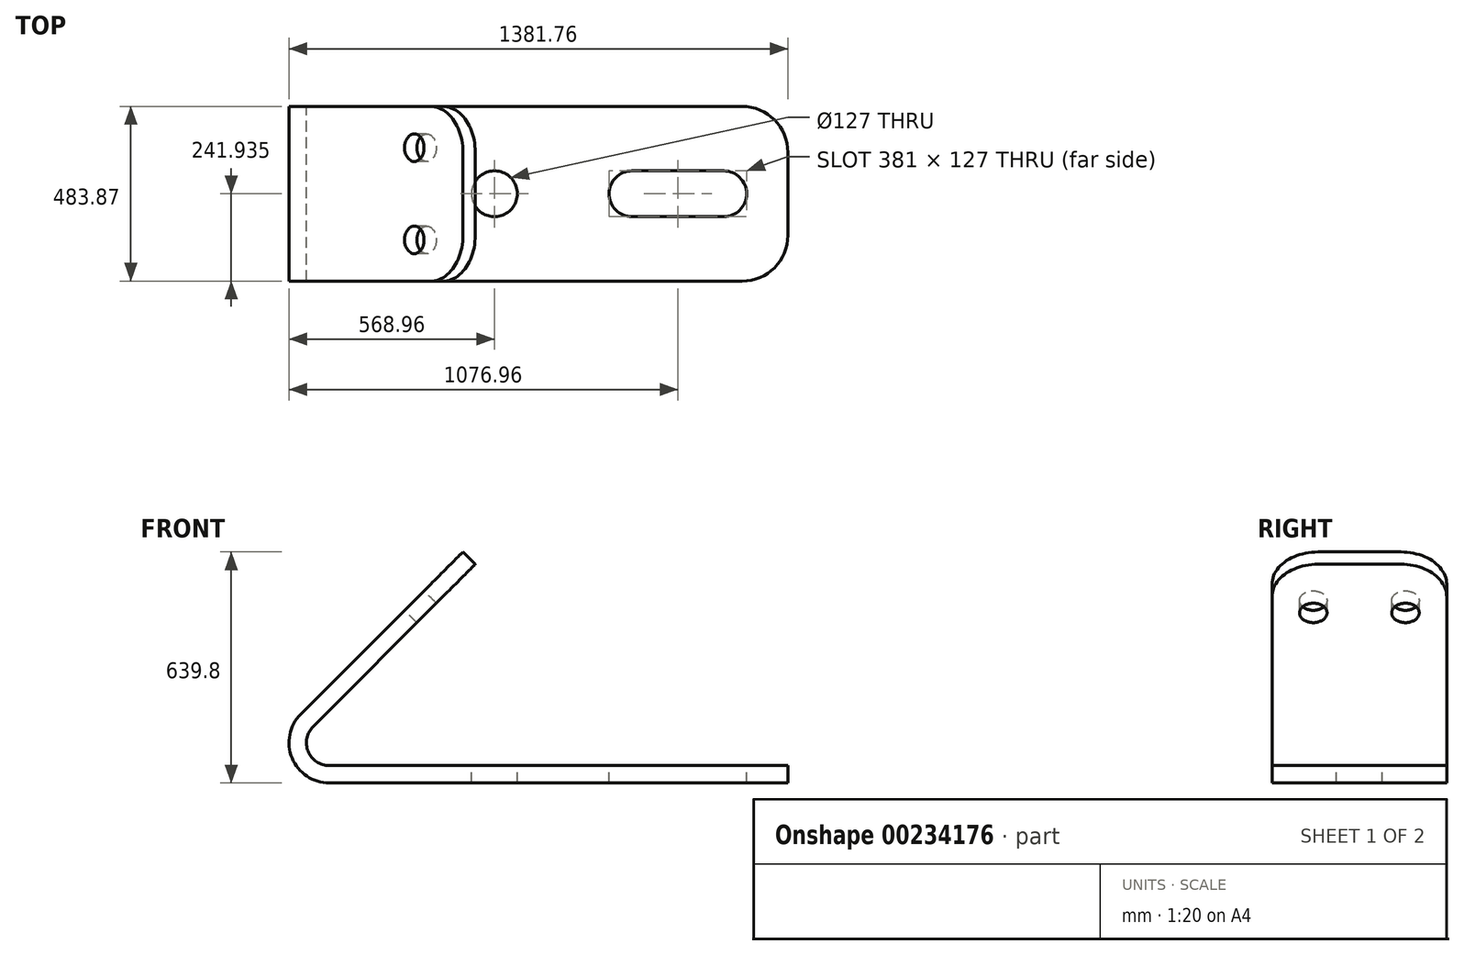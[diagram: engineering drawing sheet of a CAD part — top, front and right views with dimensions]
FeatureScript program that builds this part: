
annotation { "Feature Type Name" : "Feature", "Feature Type Description" : "" }
export const myFeature = defineFeature(function(context is Context, id is Id, definition is map)
    precondition{}
    {
        {
            var Q0;
            Q0=qCreatedBy(makeId("Front.planeOp"),FACE);
            var sketch = newSketch(context, id + "F0", { "sketchPlane" : qUnion([Q0])});
            skLineSegment(sketch, "E0", {"start": v(0, 0) * mm, "end": v(1270, 0) * mm});
            skLineSegment(sketch, "E1", {"start": v(1270, 0) * mm, "end": v(1270, 48.26) * mm});
            skLineSegment(sketch, "E2", {"start": v(1270, 48.26) * mm, "end": v(0, 48.26) * mm});
            skLineSegment(sketch, "E3", {"start": v(0, 0) * mm, "end": v(0, 111.76) * mm, "construction": true});
            skArc(sketch, "E4", {"start": v(-79.03, 190.79) * mm, "mid": v(-103.25, 69) * mm, "end": v(0, 0) * mm});
            skLineSegment(sketch, "E5", {"start": v(-79.03, 190.79) * mm, "end": v(369.99, 639.8) * mm});
            skLineSegment(sketch, "E6", {"start": v(369.99, 639.8) * mm, "end": v(404.11, 605.67) * mm});
            skArc(sketch, "E7", {"start": v(-44.9, 156.66) * mm, "mid": v(-58.67, 87.46) * mm, "end": v(0, 48.26) * mm});
            skLineSegment(sketch, "E8", {"start": v(404.11, 605.67) * mm, "end": v(-44.9, 156.66) * mm});
            skSolve(sketch);
        }
        {
            var Q0;
            Q0=qSketchRegion(id+"F0",true);
            extrude(context, id + "F1", {"entities" : qUnion([Q0]), "depth" : 483.87 * mm});
        }
        {
            var Q0;
            Q0=makeQuery(id+"F1.opExtrude","SWEPT_FACE",FACE,{"disambiguationData":[OSD([sQuery(id+"F0.wireOp",EDGE,"E5")])]});
            var sketch = newSketch(context, id + "F2", { "sketchPlane" : qUnion([Q0])});
            skCircle(sketch, "E9", {"center": v(114.3, 523.53) * mm, "radius": 38.1 * mm});
            skCircle(sketch, "E10", {"center": v(369.57, 523.53) * mm, "radius": 38.1 * mm});
            skSolve(sketch);
        }
        {
            var Q0;
            Q0=qSketchRegion(id+"F2",true);
            var Q1;
            Q1=makeQuery(id+"F1.opExtrude","SWEPT_FACE",FACE,{"disambiguationData":[OSD([sQuery(id+"F0.wireOp",EDGE,"E8")])]});
            extrude(context, id + "F3", {"entities" : qUnion([Q0]), "operationType" : NewBodyOperationType.REMOVE, "endBound" : BoundingType.UP_TO_SURFACE, "oppositeDirection" : true, "endBoundEntityFace" : qUnion([Q1]), "depth" : 25.4 * mm});
        }
        {
            var Q0;
            Q0=makeQuery(id+"F1.opExtrude","CAP_EDGE",EDGE,{"disambiguationData":[OSD([sQuery(id+"F0.wireOp",EDGE,"E6")])],"isStart":true});
            var Q1;
            Q1=makeQuery(id+"F1.opExtrude","CAP_EDGE",EDGE,{"disambiguationData":[OSD([sQuery(id+"F0.wireOp",EDGE,"E6")])],"isStart":false});
            fillet(context, id + "F4", {"entities" : qUnion([Q0, Q1]), "radius" : 127 * mm, "tangentPropagation" : true, "allowEdgeOverflow" : false});
        }
        {
            var Q0;
            Q0=makeQuery(id+"F1.opExtrude","SWEPT_FACE",FACE,{"disambiguationData":[OSD([sQuery(id+"F0.wireOp",EDGE,"E2")])]});
            var sketch = newSketch(context, id + "F5", { "sketchPlane" : qUnion([Q0])});
            skLineSegment(sketch, "E11", {"start": v(457.2, -241.94) * mm, "end": v(1270, -241.94) * mm, "construction": true});
            skCircle(sketch, "E12", {"center": v(457.2, -241.94) * mm, "radius": 63.5 * mm});
            skArc(sketch, "E13", {"start": v(1092.2, -305.44) * mm, "mid": v(1155.7, -241.94) * mm, "end": v(1092.2, -178.44) * mm});
            skLineSegment(sketch, "E14", {"start": v(1092.2, -178.44) * mm, "end": v(965.2, -178.44) * mm});
            skLineSegment(sketch, "E15", {"start": v(1092.2, -305.44) * mm, "end": v(965.2, -305.44) * mm});
            skLineSegment(sketch, "E16", {"start": v(965.2, -305.44) * mm, "end": v(965.2, -77.54) * mm, "construction": true});
            skLineSegment(sketch, "E17.MirrorCS", {"start": v(838.2, -178.44) * mm, "end": v(965.2, -178.44) * mm});
            skArc(sketch, "E18.MirrorCS", {"start": v(838.2, -305.44) * mm, "mid": v(774.7, -241.94) * mm, "end": v(838.2, -178.44) * mm});
            skLineSegment(sketch, "E19.MirrorCS", {"start": v(838.2, -305.44) * mm, "end": v(965.2, -305.44) * mm});
            skSolve(sketch);
        }
        {
            var Q0;
            Q0=qSketchRegion(id+"F5",true);
            extrude(context, id + "F6", {"entities" : qUnion([Q0]), "operationType" : NewBodyOperationType.REMOVE, "endBound" : BoundingType.THROUGH_ALL, "oppositeDirection" : true, "depth" : 25.4 * mm});
        }
        {
            var Q0;
            Q0=makeQuery(id+"F1.opExtrude","CAP_EDGE",EDGE,{"disambiguationData":[OSD([sQuery(id+"F0.wireOp",EDGE,"E1")])],"isStart":false});
            var Q1;
            Q1=makeQuery(id+"F1.opExtrude","CAP_EDGE",EDGE,{"disambiguationData":[OSD([sQuery(id+"F0.wireOp",EDGE,"E1")])],"isStart":true});
            fillet(context, id + "F7", {"entities" : qUnion([Q0, Q1]), "radius" : 127 * mm, "tangentPropagation" : true, "allowEdgeOverflow" : false});
        }
    });
